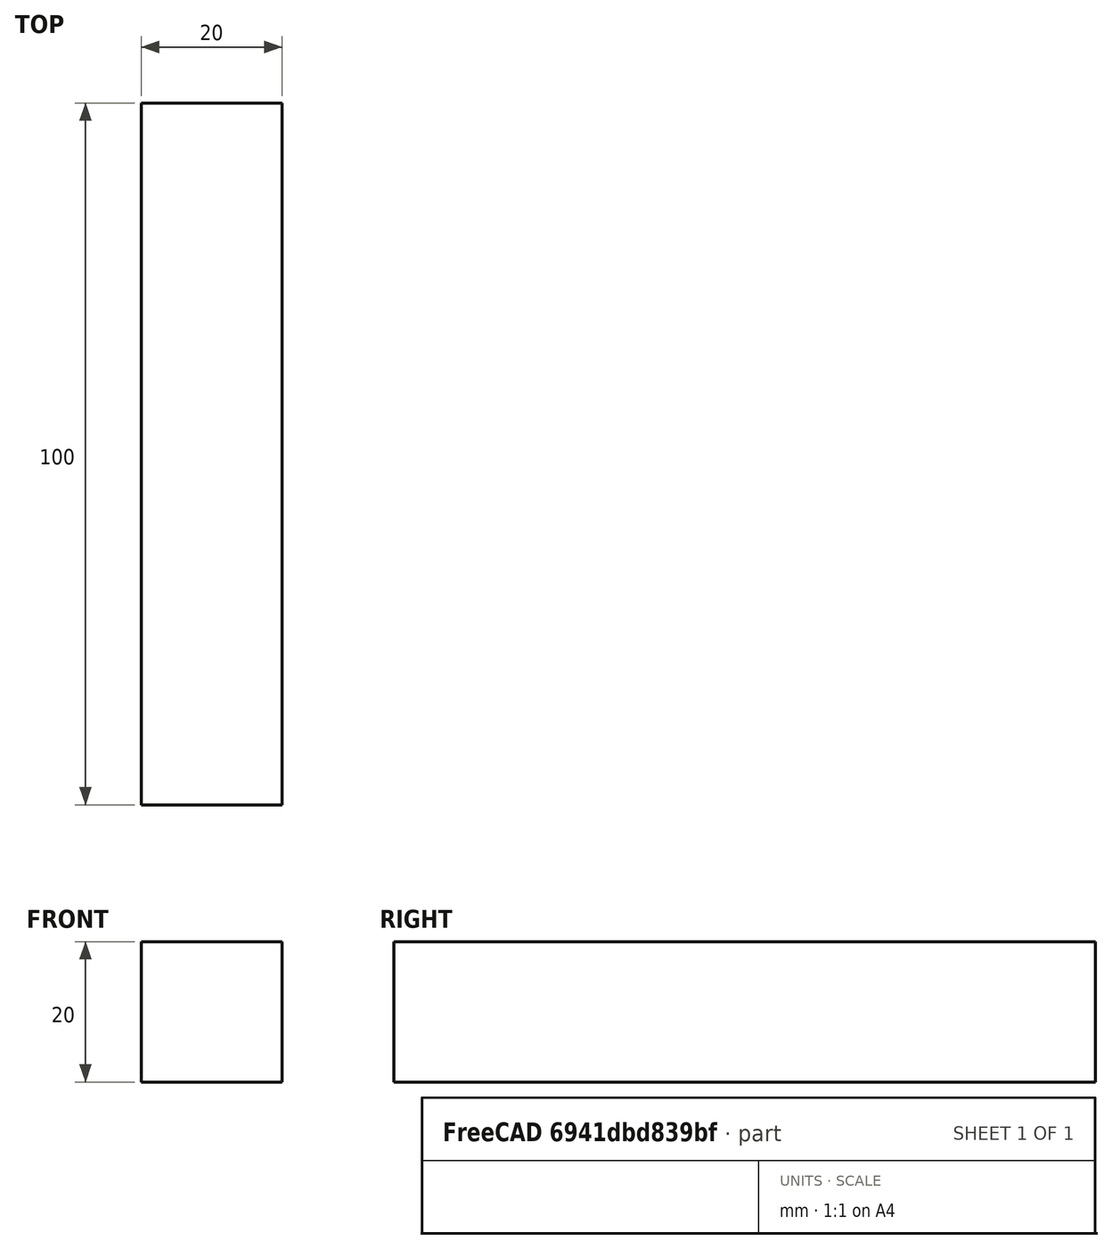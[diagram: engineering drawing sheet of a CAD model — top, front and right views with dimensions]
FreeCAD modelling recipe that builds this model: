
FCSTD DOCUMENT  (FreeCAD 0.19R24291 (Git))
Label: rail
License: All rights reserved
LicenseURL: http://en.wikipedia.org/wiki/All_rights_reserved
objects: Sketcher::SketchObject×1, PartDesign::Pad×1, PartDesign::Body×1
note: 4 computed .brp shape members not serialized (recipe doc carries the construction recipe); baked Part::Feature solids carry a one-line shape summary decoded from their .brp

FEATURE [Sketcher::SketchObject] Sketch
  FullyConstrained = true
  MapMode = 5
  Placement = pos=(0,0,0) rot=(1,0,0;1.5708rad)
  Support = -> [XZ_Plane]
  sketch-geometry (4):
    g0: LineSegment StartX=0 StartY=0 StartZ=0 EndX=20 EndY=0 EndZ=0
    g1: LineSegment StartX=20 StartY=0 StartZ=0 EndX=20 EndY=20 EndZ=0
    g2: LineSegment StartX=20 StartY=20 StartZ=0 EndX=0 EndY=20 EndZ=0
    g3: LineSegment StartX=0 StartY=20 StartZ=0 EndX=0 EndY=0 EndZ=0
  constraints (11):
    c: Coincident(g0,g1)
    c: Coincident(g1,g2)
    c: Coincident(g2,g3)
    c: Coincident(g3,g0)
    c: Horizontal(g0)
    c: Horizontal(g2)
    c: Vertical(g1)
    c: Vertical(g3)
    c: Coincident(g0,g-1)
    c: DistanceX(g2,g2) = 20
    c: DistanceY(g1,g1) = 20
FEATURE [PartDesign::Pad] Pad
  Direction = (1,1,1)
  Length = 100
  Length2 = 100
  Placement = pos=(0,0,0) rot=(1,0,0;1.5708rad)
  Profile = -> Sketch
  Type = 0
FEATURE [PartDesign::Body] Body
  Group = -> [Sketch,Pad]
  Origin = -> Origin
  Tip = -> Pad
